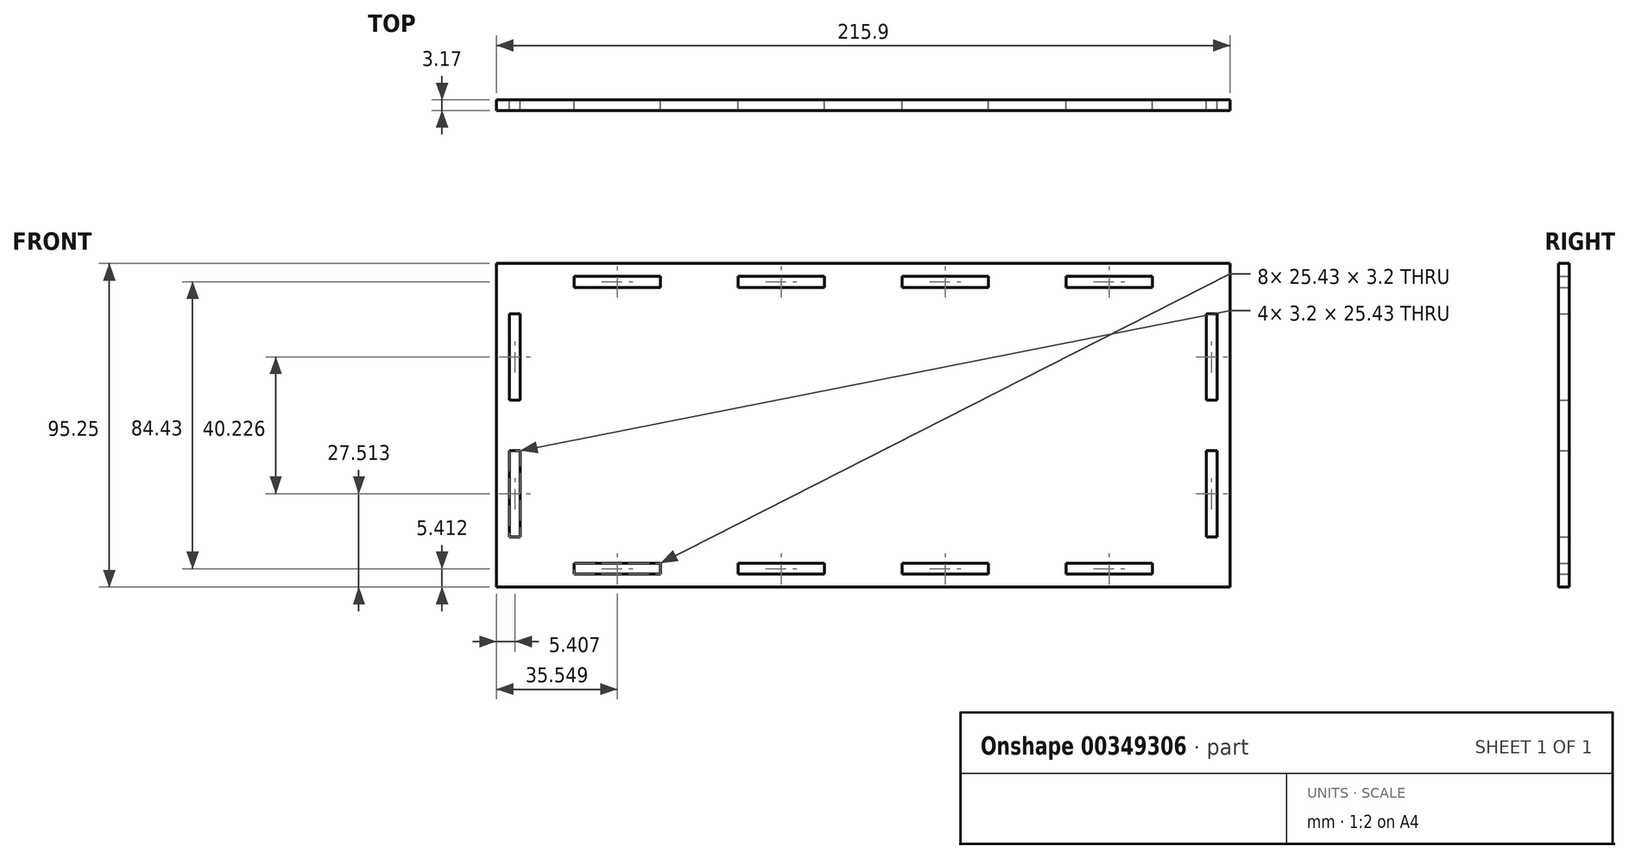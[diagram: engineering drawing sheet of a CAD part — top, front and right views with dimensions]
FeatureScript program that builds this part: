
annotation { "Feature Type Name" : "Feature", "Feature Type Description" : "" }
export const myFeature = defineFeature(function(context is Context, id is Id, definition is map)
    precondition{}
    {
        {
            var Q0;
            Q0=qCreatedBy(makeId("Front.planeOp"),FACE);
            var sketch = newSketch(context, id + "F0", { "sketchPlane" : qUnion([Q0])});
            skLineSegment(sketch, "E0.bottom", {"start": v(-97.14, 44.33) * mm, "end": v(118.76, 44.33) * mm});
            skLineSegment(sketch, "E0.top", {"start": v(-97.14, -50.92) * mm, "end": v(118.76, -50.92) * mm});
            skLineSegment(sketch, "E0.left", {"start": v(-97.14, 44.33) * mm, "end": v(-97.14, -50.92) * mm});
            skLineSegment(sketch, "E0.right", {"start": v(118.76, 44.33) * mm, "end": v(118.76, -50.92) * mm});
            skLineSegment(sketch, "E1.bottom", {"start": v(-74.3, 40.52) * mm, "end": v(-48.88, 40.52) * mm});
            skLineSegment(sketch, "E1.top", {"start": v(-74.3, 37.32) * mm, "end": v(-48.88, 37.32) * mm});
            skLineSegment(sketch, "E1.left", {"start": v(-74.3, 40.52) * mm, "end": v(-74.3, 37.32) * mm});
            skLineSegment(sketch, "E1.right", {"start": v(-48.88, 40.52) * mm, "end": v(-48.88, 37.32) * mm});
            skLineSegment(sketch, "E2.bottom", {"start": v(-26.04, 40.52) * mm, "end": v(-0.61, 40.52) * mm});
            skLineSegment(sketch, "E2.top", {"start": v(-26.04, 37.32) * mm, "end": v(-0.61, 37.32) * mm});
            skLineSegment(sketch, "E2.left", {"start": v(-26.04, 40.52) * mm, "end": v(-26.04, 37.32) * mm});
            skLineSegment(sketch, "E2.right", {"start": v(-0.61, 40.52) * mm, "end": v(-0.61, 37.32) * mm});
            skLineSegment(sketch, "E3.bottom", {"start": v(70.5, 40.52) * mm, "end": v(95.92, 40.52) * mm});
            skLineSegment(sketch, "E3.top", {"start": v(70.5, 37.32) * mm, "end": v(95.92, 37.32) * mm});
            skLineSegment(sketch, "E3.left", {"start": v(70.5, 40.52) * mm, "end": v(70.5, 37.32) * mm});
            skLineSegment(sketch, "E3.right", {"start": v(95.92, 40.52) * mm, "end": v(95.92, 37.32) * mm});
            skLineSegment(sketch, "E4.bottom", {"start": v(22.23, 40.52) * mm, "end": v(47.65, 40.52) * mm});
            skLineSegment(sketch, "E4.top", {"start": v(22.23, 37.32) * mm, "end": v(47.65, 37.32) * mm});
            skLineSegment(sketch, "E4.left", {"start": v(22.23, 40.52) * mm, "end": v(22.23, 37.32) * mm});
            skLineSegment(sketch, "E4.right", {"start": v(47.65, 40.52) * mm, "end": v(47.65, 37.32) * mm});
            skLineSegment(sketch, "E5.bottom", {"start": v(-74.3, -43.9) * mm, "end": v(-48.88, -43.9) * mm});
            skLineSegment(sketch, "E5.top", {"start": v(-74.3, -47.1) * mm, "end": v(-48.88, -47.1) * mm});
            skLineSegment(sketch, "E5.left", {"start": v(-74.3, -43.9) * mm, "end": v(-74.3, -47.1) * mm});
            skLineSegment(sketch, "E5.right", {"start": v(-48.88, -43.9) * mm, "end": v(-48.88, -47.1) * mm});
            skLineSegment(sketch, "E6.bottom", {"start": v(-26.04, -43.9) * mm, "end": v(-0.61, -43.9) * mm});
            skLineSegment(sketch, "E6.top", {"start": v(-26.04, -47.1) * mm, "end": v(-0.61, -47.1) * mm});
            skLineSegment(sketch, "E6.left", {"start": v(-26.04, -43.9) * mm, "end": v(-26.04, -47.1) * mm});
            skLineSegment(sketch, "E6.right", {"start": v(-0.61, -43.9) * mm, "end": v(-0.61, -47.1) * mm});
            skLineSegment(sketch, "E7.bottom", {"start": v(70.5, -43.9) * mm, "end": v(95.92, -43.9) * mm});
            skLineSegment(sketch, "E7.top", {"start": v(70.5, -47.1) * mm, "end": v(95.92, -47.1) * mm});
            skLineSegment(sketch, "E7.left", {"start": v(70.5, -43.9) * mm, "end": v(70.5, -47.1) * mm});
            skLineSegment(sketch, "E7.right", {"start": v(95.92, -43.9) * mm, "end": v(95.92, -47.1) * mm});
            skLineSegment(sketch, "E8.bottom", {"start": v(22.23, -43.9) * mm, "end": v(47.65, -43.9) * mm});
            skLineSegment(sketch, "E8.top", {"start": v(22.23, -47.1) * mm, "end": v(47.65, -47.1) * mm});
            skLineSegment(sketch, "E8.left", {"start": v(22.23, -43.9) * mm, "end": v(22.23, -47.1) * mm});
            skLineSegment(sketch, "E8.right", {"start": v(47.65, -43.9) * mm, "end": v(47.65, -47.1) * mm});
            skLineSegment(sketch, "E9.bottom", {"start": v(111.75, 29.53) * mm, "end": v(114.95, 29.53) * mm});
            skLineSegment(sketch, "E9.top", {"start": v(111.75, 4.1) * mm, "end": v(114.95, 4.1) * mm});
            skLineSegment(sketch, "E9.left", {"start": v(111.75, 29.53) * mm, "end": v(111.75, 4.1) * mm});
            skLineSegment(sketch, "E9.right", {"start": v(114.95, 29.53) * mm, "end": v(114.95, 4.1) * mm});
            skLineSegment(sketch, "E10.bottom", {"start": v(111.75, -10.7) * mm, "end": v(114.95, -10.7) * mm});
            skLineSegment(sketch, "E10.top", {"start": v(111.75, -36.12) * mm, "end": v(114.95, -36.12) * mm});
            skLineSegment(sketch, "E10.left", {"start": v(111.75, -10.7) * mm, "end": v(111.75, -36.12) * mm});
            skLineSegment(sketch, "E10.right", {"start": v(114.95, -10.7) * mm, "end": v(114.95, -36.12) * mm});
            skLineSegment(sketch, "E11.bottom", {"start": v(-93.33, 29.53) * mm, "end": v(-90.13, 29.53) * mm});
            skLineSegment(sketch, "E11.top", {"start": v(-93.33, 4.1) * mm, "end": v(-90.13, 4.1) * mm});
            skLineSegment(sketch, "E11.left", {"start": v(-93.33, 29.53) * mm, "end": v(-93.33, 4.1) * mm});
            skLineSegment(sketch, "E11.right", {"start": v(-90.13, 29.53) * mm, "end": v(-90.13, 4.1) * mm});
            skLineSegment(sketch, "E12.bottom", {"start": v(-93.33, -10.7) * mm, "end": v(-90.13, -10.7) * mm});
            skLineSegment(sketch, "E12.top", {"start": v(-93.33, -36.12) * mm, "end": v(-90.13, -36.12) * mm});
            skLineSegment(sketch, "E12.left", {"start": v(-93.33, -10.7) * mm, "end": v(-93.33, -36.12) * mm});
            skLineSegment(sketch, "E12.right", {"start": v(-90.13, -10.7) * mm, "end": v(-90.13, -36.12) * mm});
            skSolve(sketch);
        }
        {
            var Q0;
            Q0=makeQuery(id+"F0.imprint","IMPRINT",FACE,{"disambiguationData":[TD([[makeQuery(id+"F0.imprint","IMPRINT",EDGE,{"derivedFrom":sQuery(id+"F0.wireOp",EDGE,"E0.bottom")}),-1.0]])]});
            extrude(context, id + "F1", {"entities" : qUnion([Q0]), "depth" : 3.17 * mm});
        }
    });
